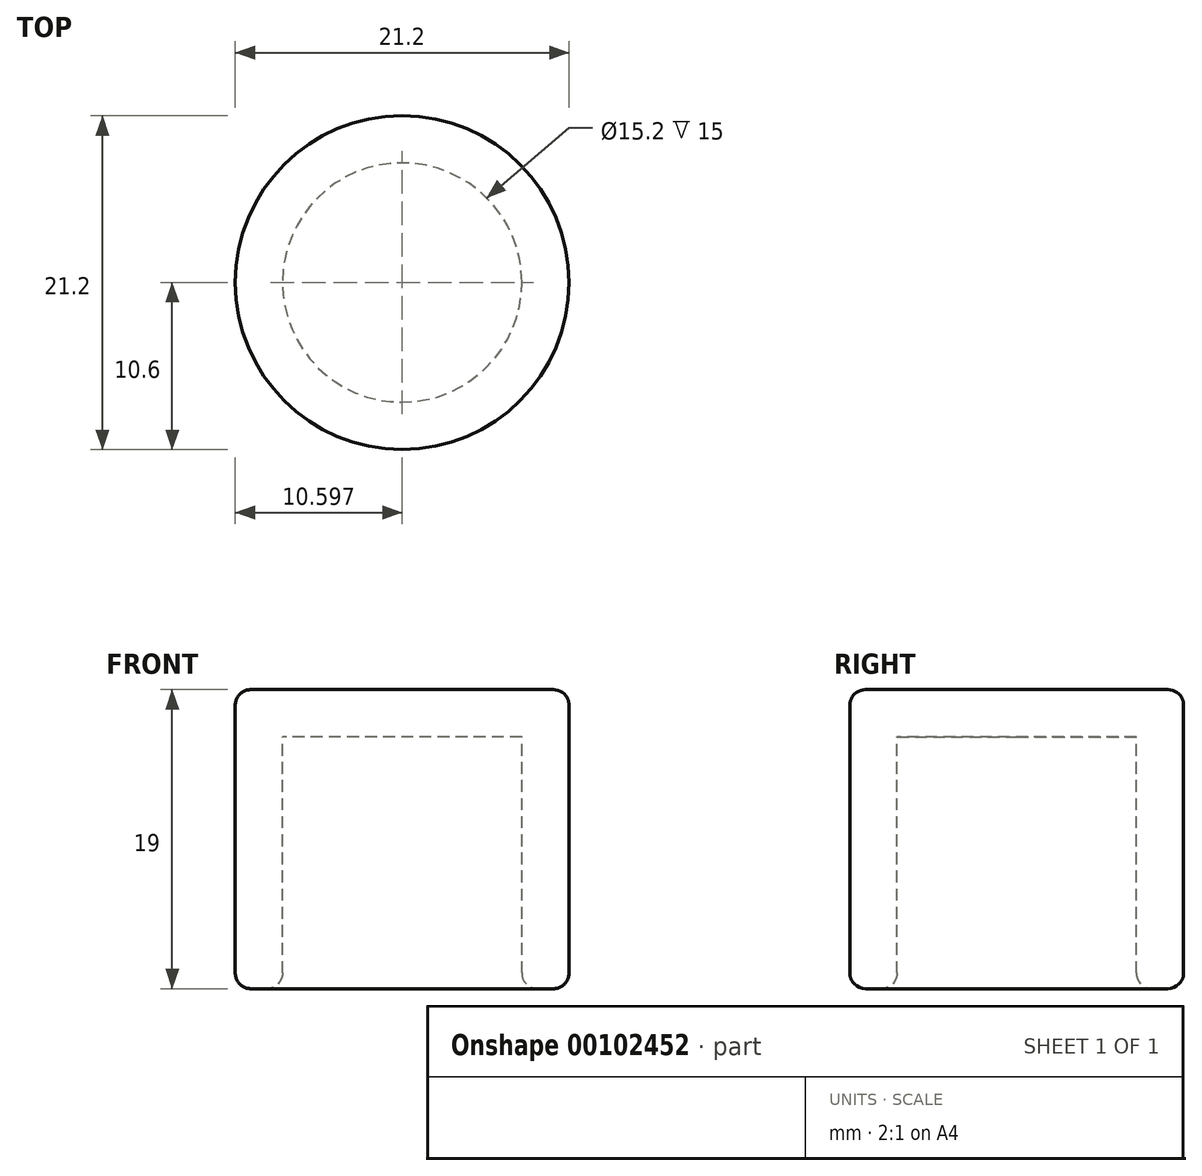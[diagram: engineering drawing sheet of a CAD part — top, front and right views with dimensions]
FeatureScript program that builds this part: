
annotation { "Feature Type Name" : "Feature", "Feature Type Description" : "" }
export const myFeature = defineFeature(function(context is Context, id is Id, definition is map)
    precondition{}
    {
        {
            var Q0;
            Q0=qCreatedBy(makeId("Front.planeOp"),FACE);
            var sketch = newSketch(context, id + "F0", { "sketchPlane" : qUnion([Q0])});
            skLineSegment(sketch, "E0", {"start": v(-1.53, -5.94) * mm, "end": v(-1.53, -21.94) * mm});
            skLineSegment(sketch, "E1", {"start": v(-1.53, -21.94) * mm, "end": v(-4.53, -21.94) * mm});
            skLineSegment(sketch, "E2", {"start": v(6.07, -2.94) * mm, "end": v(6.07, -5.94) * mm});
            skLineSegment(sketch, "E3", {"start": v(-1.53, -5.94) * mm, "end": v(6.07, -5.94) * mm});
            skLineSegment(sketch, "E4", {"start": v(-4.53, -2.94) * mm, "end": v(6.07, -2.94) * mm});
            skLineSegment(sketch, "E5", {"start": v(-4.53, -21.94) * mm, "end": v(-4.53, -2.94) * mm});
            skSolve(sketch);
        }
        {
            var Q0;
            Q0=makeQuery(id+"F0.imprint","IMPRINT",FACE,{"disambiguationData":[TD([[makeQuery(id+"F0.imprint","IMPRINT",EDGE,{"derivedFrom":sQuery(id+"F0.wireOp",EDGE,"E0")}),-1.0]])]});
            var Q1;
            Q1=sQuery(id+"F0.wireOp",EDGE,"E2");
            revolve(context, id + "F1", {"entities" : qUnion([Q0]), "axis" : qUnion([Q1]), "revolveType" : RevolveType.FULL});
        }
        {
            var Q0;
            Q0=makeQuery(id+"F1.opRevolve","SWEPT_FACE",FACE,{"disambiguationData":[OSD([sQuery(id+"F0.wireOp",EDGE,"E1")])]});
            var Q1;
            Q1=makeQuery(id+"F1.opRevolve","SWEPT_FACE",FACE,{"disambiguationData":[OSD([sQuery(id+"F0.wireOp",EDGE,"E5")])]});
            fillet(context, id + "F2", {"entities" : qUnion([Q0, Q1]), "radius" : 1 * mm, "tangentPropagation" : true, "allowEdgeOverflow" : false});
        }
    });
